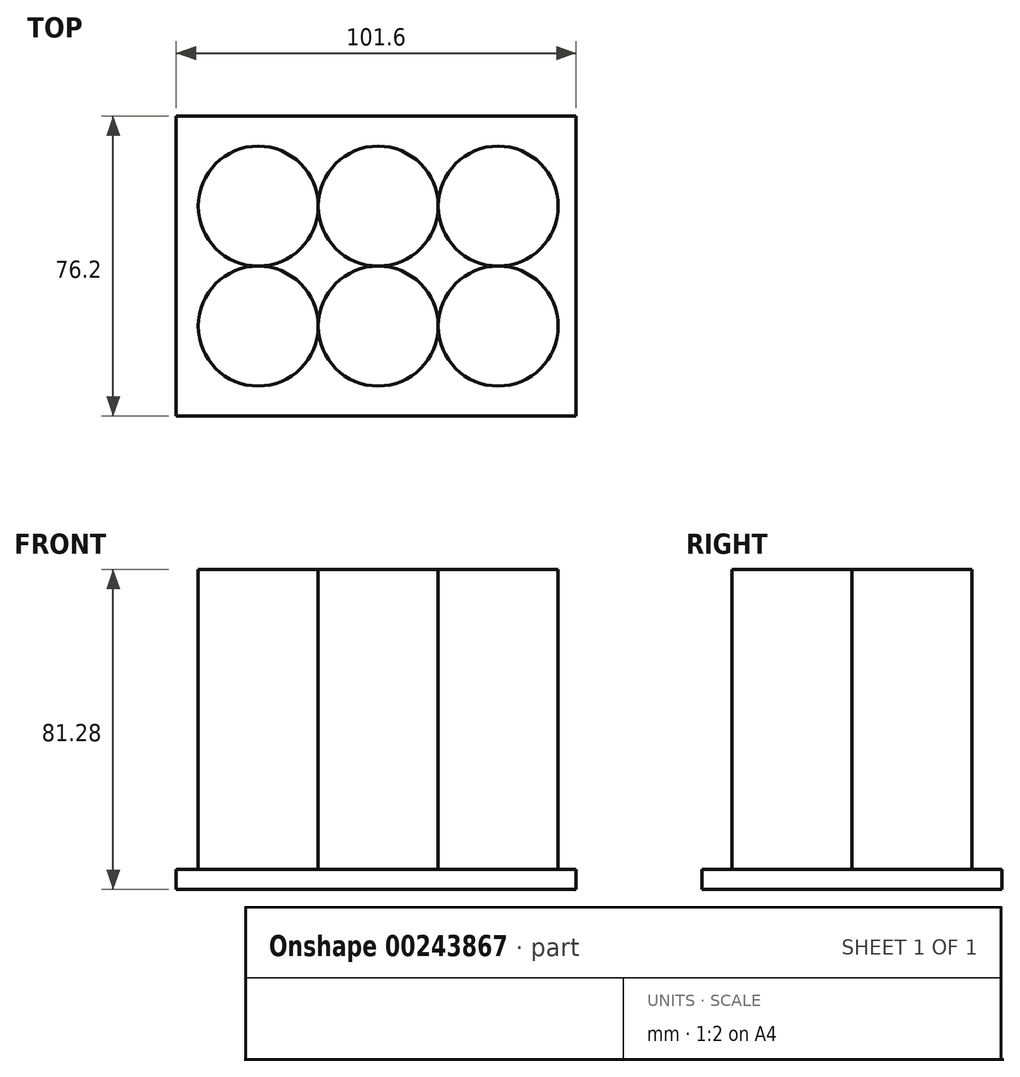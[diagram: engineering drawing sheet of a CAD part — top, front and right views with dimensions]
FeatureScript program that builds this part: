
annotation { "Feature Type Name" : "Feature", "Feature Type Description" : "" }
export const myFeature = defineFeature(function(context is Context, id is Id, definition is map)
    precondition{}
    {
        {
            var Q0;
            Q0=qCreatedBy(makeId("Top.planeOp"),FACE);
            var sketch = newSketch(context, id + "F0", { "sketchPlane" : qUnion([Q0])});
            skCircle(sketch, "E0", {"center": v(-29.97, -15.25) * mm, "radius": 15.24 * mm});
            skCircle(sketch, "E1", {"center": v(0.51, -15.25) * mm, "radius": 15.24 * mm});
            skCircle(sketch, "E2", {"center": v(31, -15.25) * mm, "radius": 15.24 * mm});
            skLineSegment(sketch, "E3", {"start": v(-29.97, -15.25) * mm, "end": v(50.03, -15.25) * mm, "construction": true});
            skCircle(sketch, "E4", {"center": v(-29.97, 15.23) * mm, "radius": 15.24 * mm});
            skCircle(sketch, "E5", {"center": v(0.51, 15.23) * mm, "radius": 15.24 * mm});
            skCircle(sketch, "E6", {"center": v(31, 15.23) * mm, "radius": 15.24 * mm});
            skLineSegment(sketch, "E7", {"start": v(-29.97, 15.23) * mm, "end": v(34.43, 15.23) * mm, "construction": true});
            skLineSegment(sketch, "E8", {"start": v(-29.97, 15.23) * mm, "end": v(-29.97, -15.25) * mm, "construction": true});
            skSolve(sketch);
        }
        {
            var Q0;
            {var subQ0=sQuery(id+"F0.wireOp",EDGE,"ICpDPUjX-ivMe-23Ei-ieje-qIsjfVPonkm3");var subQ1=makeQuery(id+"F0.imprint","INTERSECT",VERTEX,{"derivedFrom":[subQ0,sQuery(id+"F0.wireOp",EDGE,"1585de0c-b4fc-4455-9636-1ccd38715f07")]});Q0=makeQuery(id+"F0.imprint","IMPRINT",FACE,{"disambiguationData":[TD([[makeQuery(id+"F0.imprint","IMPRINT",EDGE,{"disambiguationData":[TD([[subQ1,-1.0]])],"derivedFrom":subQ0}),1.0]])]});}
            var Q1;
            {var subQ0=sQuery(id+"F0.wireOp",EDGE,"1585de0c-b4fc-4455-9636-1ccd38715f07");var subQ1=makeQuery(id+"F0.imprint","INTERSECT",VERTEX,{"derivedFrom":[sQuery(id+"F0.wireOp",EDGE,"ICpDPUjX-ivMe-23Ei-ieje-qIsjfVPonkm3"),subQ0]});Q1=makeQuery(id+"F0.imprint","IMPRINT",FACE,{"disambiguationData":[TD([[makeQuery(id+"F0.imprint","IMPRINT",EDGE,{"disambiguationData":[TD([[subQ1,1.0]])],"derivedFrom":subQ0}),1.0]])]});}
            var Q2;
            {var subQ0=sQuery(id+"F0.wireOp",EDGE,"8cf919d0-c88a-4376-973f-18324e1bfcb2");var subQ1=makeQuery(id+"F0.imprint","INTERSECT",VERTEX,{"derivedFrom":[sQuery(id+"F0.wireOp",EDGE,"1585de0c-b4fc-4455-9636-1ccd38715f07"),subQ0]});Q2=makeQuery(id+"F0.imprint","IMPRINT",FACE,{"disambiguationData":[TD([[makeQuery(id+"F0.imprint","IMPRINT",EDGE,{"disambiguationData":[TD([[subQ1,-1.0]])],"derivedFrom":subQ0}),1.0]])]});}
            var Q3;
            {var subQ0=sQuery(id+"F0.wireOp",EDGE,"0c448a11-c32a-4d7b-bc3d-f4b18554e8e6");var subQ1=makeQuery(id+"F0.imprint","INTERSECT",VERTEX,{"derivedFrom":[sQuery(id+"F0.wireOp",EDGE,"8cf919d0-c88a-4376-973f-18324e1bfcb2"),subQ0]});Q3=makeQuery(id+"F0.imprint","IMPRINT",FACE,{"disambiguationData":[TD([[makeQuery(id+"F0.imprint","IMPRINT",EDGE,{"disambiguationData":[TD([[subQ1,-1.0]])],"derivedFrom":subQ0}),1.0]])]});}
            var Q4;
            {var subQ0=sQuery(id+"F0.wireOp",EDGE,"877ee094-fdc9-495d-ab0e-c5a52c05f9cd");var subQ4=makeQuery(id+"F0.imprint","INTERSECT",VERTEX,{"derivedFrom":[sQuery(id+"F0.wireOp",EDGE,"8cf919d0-c88a-4376-973f-18324e1bfcb2"),subQ0]});Q4=makeQuery(id+"F0.imprint","IMPRINT",FACE,{"disambiguationData":[TD([[makeQuery(id+"F0.imprint","IMPRINT",EDGE,{"disambiguationData":[TD([[subQ4,1.0]])],"derivedFrom":subQ0}),1.0]])]});}
            var Q5;
            {var subQ0=sQuery(id+"F0.wireOp",EDGE,"d8245553-00ec-417b-91d8-0db8256ae251");var subQ4=makeQuery(id+"F0.imprint","INTERSECT",VERTEX,{"derivedFrom":[sQuery(id+"F0.wireOp",EDGE,"1585de0c-b4fc-4455-9636-1ccd38715f07"),subQ0]});Q5=makeQuery(id+"F0.imprint","IMPRINT",FACE,{"disambiguationData":[TD([[makeQuery(id+"F0.imprint","IMPRINT",EDGE,{"disambiguationData":[TD([[subQ4,1.0]])],"derivedFrom":subQ0}),1.0]])]});}
            var Q6;
            {var subQ0=sQuery(id+"F0.wireOp",EDGE,"E0");var subQ1=makeQuery(id+"F0.imprint","INTERSECT",VERTEX,{"derivedFrom":[sQuery(id+"F0.wireOp",EDGE,"d8245553-00ec-417b-91d8-0db8256ae251"),subQ0]});Q6=makeQuery(id+"F0.imprint","IMPRINT",FACE,{"disambiguationData":[TD([[makeQuery(id+"F0.imprint","IMPRINT",EDGE,{"disambiguationData":[TD([[subQ1,1.0]])],"derivedFrom":subQ0}),1.0]])]});}
            var Q7;
            {var subQ0=sQuery(id+"F0.wireOp",EDGE,"E1");var subQ1=makeQuery(id+"F0.imprint","INTERSECT",VERTEX,{"derivedFrom":[subQ0,sQuery(id+"F0.wireOp",EDGE,"E2")]});Q7=makeQuery(id+"F0.imprint","IMPRINT",FACE,{"disambiguationData":[TD([[makeQuery(id+"F0.imprint","IMPRINT",EDGE,{"disambiguationData":[TD([[subQ1,-1.0]])],"derivedFrom":subQ0}),1.0]])]});}
            var Q8;
            {var subQ0=sQuery(id+"F0.wireOp",EDGE,"E2");var subQ1=makeQuery(id+"F0.imprint","INTERSECT",VERTEX,{"derivedFrom":[sQuery(id+"F0.wireOp",EDGE,"0c448a11-c32a-4d7b-bc3d-f4b18554e8e6"),subQ0]});Q8=makeQuery(id+"F0.imprint","IMPRINT",FACE,{"disambiguationData":[TD([[makeQuery(id+"F0.imprint","IMPRINT",EDGE,{"disambiguationData":[TD([[subQ1,-1.0]])],"derivedFrom":subQ0}),1.0]])]});}
            var Q9;
            {var subQ0=sQuery(id+"F0.wireOp",EDGE,"E4");var subQ1=makeQuery(id+"F0.imprint","INTERSECT",VERTEX,{"derivedFrom":[sQuery(id+"F0.wireOp",EDGE,"E0"),subQ0]});Q9=makeQuery(id+"F0.imprint","IMPRINT",FACE,{"disambiguationData":[TD([[makeQuery(id+"F0.imprint","IMPRINT",EDGE,{"disambiguationData":[TD([[subQ1,1.0]])],"derivedFrom":subQ0}),1.0]])]});}
            var Q10;
            {var subQ0=sQuery(id+"F0.wireOp",EDGE,"E5");var subQ1=makeQuery(id+"F0.imprint","INTERSECT",VERTEX,{"derivedFrom":[sQuery(id+"F0.wireOp",EDGE,"E4"),subQ0]});Q10=makeQuery(id+"F0.imprint","IMPRINT",FACE,{"disambiguationData":[TD([[makeQuery(id+"F0.imprint","IMPRINT",EDGE,{"disambiguationData":[TD([[subQ1,1.0]])],"derivedFrom":subQ0}),1.0]])]});}
            var Q11;
            {var subQ0=sQuery(id+"F0.wireOp",EDGE,"E6");var subQ1=makeQuery(id+"F0.imprint","INTERSECT",VERTEX,{"derivedFrom":[sQuery(id+"F0.wireOp",EDGE,"E2"),subQ0]});Q11=makeQuery(id+"F0.imprint","IMPRINT",FACE,{"disambiguationData":[TD([[makeQuery(id+"F0.imprint","IMPRINT",EDGE,{"disambiguationData":[TD([[subQ1,1.0]])],"derivedFrom":subQ0}),1.0]])]});}
            var Q12;
            Q12=sQuery(id+"F0.wireOp",EDGE,"877ee094-fdc9-495d-ab0e-c5a52c05f9cd");
            var Q13;
            Q13=sQuery(id+"F0.wireOp",EDGE,"ICpDPUjX-ivMe-23Ei-ieje-qIsjfVPonkm3");
            var Q14;
            Q14=sQuery(id+"F0.wireOp",EDGE,"E2");
            var Q15;
            Q15=sQuery(id+"F0.wireOp",EDGE,"E1");
            var Q16;
            Q16=sQuery(id+"F0.wireOp",EDGE,"E0");
            var Q17;
            Q17=sQuery(id+"F0.wireOp",EDGE,"0c448a11-c32a-4d7b-bc3d-f4b18554e8e6");
            var Q18;
            Q18=sQuery(id+"F0.wireOp",EDGE,"d8245553-00ec-417b-91d8-0db8256ae251");
            var Q19;
            Q19=sQuery(id+"F0.wireOp",EDGE,"8cf919d0-c88a-4376-973f-18324e1bfcb2");
            var Q20;
            Q20=sQuery(id+"F0.wireOp",EDGE,"1585de0c-b4fc-4455-9636-1ccd38715f07");
            extrude(context, id + "F1", {"entities" : qUnion([Q0, Q1, Q2, Q3, Q4, Q5, Q6, Q7, Q8, Q9, Q10, Q11]), "surfaceEntities" : qUnion([Q12, Q13, Q14, Q15, Q16, Q17, Q18, Q19, Q20]), "depth" : 76.2 * mm});
        }
        {
            var Q0;
            Q0=qCreatedBy(makeId("Front.planeOp"),FACE);
            var sketch = newSketch(context, id + "F2", { "sketchPlane" : qUnion([Q0])});
            skLineSegment(sketch, "E9.bottom", {"start": v(50.8, 0) * mm, "end": v(-50.8, 0) * mm});
            skLineSegment(sketch, "E9.top", {"start": v(50.8, -5.08) * mm, "end": v(-50.8, -5.08) * mm});
            skLineSegment(sketch, "E9.left", {"start": v(50.8, 0) * mm, "end": v(50.8, -5.08) * mm});
            skLineSegment(sketch, "E9.right", {"start": v(-50.8, 0) * mm, "end": v(-50.8, -5.08) * mm});
            skLineSegment(sketch, "E10", {"start": v(-50.8, 40.64) * mm, "end": v(-50.8, -5.08) * mm, "construction": true});
            skSolve(sketch);
        }
        {
            var Q0;
            Q0=makeQuery(id+"F2.imprint","IMPRINT",FACE,{"disambiguationData":[TD([[makeQuery(id+"F2.imprint","IMPRINT",EDGE,{"derivedFrom":sQuery(id+"F2.wireOp",EDGE,"E9.bottom")}),1.0]])]});
            var Q1;
            Q1=makeQuery(id+"F2.imprint","IMPRINT",FACE,{"disambiguationData":[TD([[makeQuery(id+"F2.imprint","IMPRINT",EDGE,{"derivedFrom":sQuery(id+"F2.wireOp",EDGE,"b8d46107-f48f-4c03-8077-e383a4ff9cb9.bottom")}),1.0]])]});
            var Q2;
            Q2=sQuery(id+"F2.wireOp",EDGE,"E9.bottom");
            extrude(context, id + "F3", {"entities" : qUnion([Q0, Q1]), "surfaceEntities" : qUnion([Q2]), "endBound" : BoundingType.SYMMETRIC, "oppositeDirection" : true, "depth" : 76.2 * mm});
        }
    });
